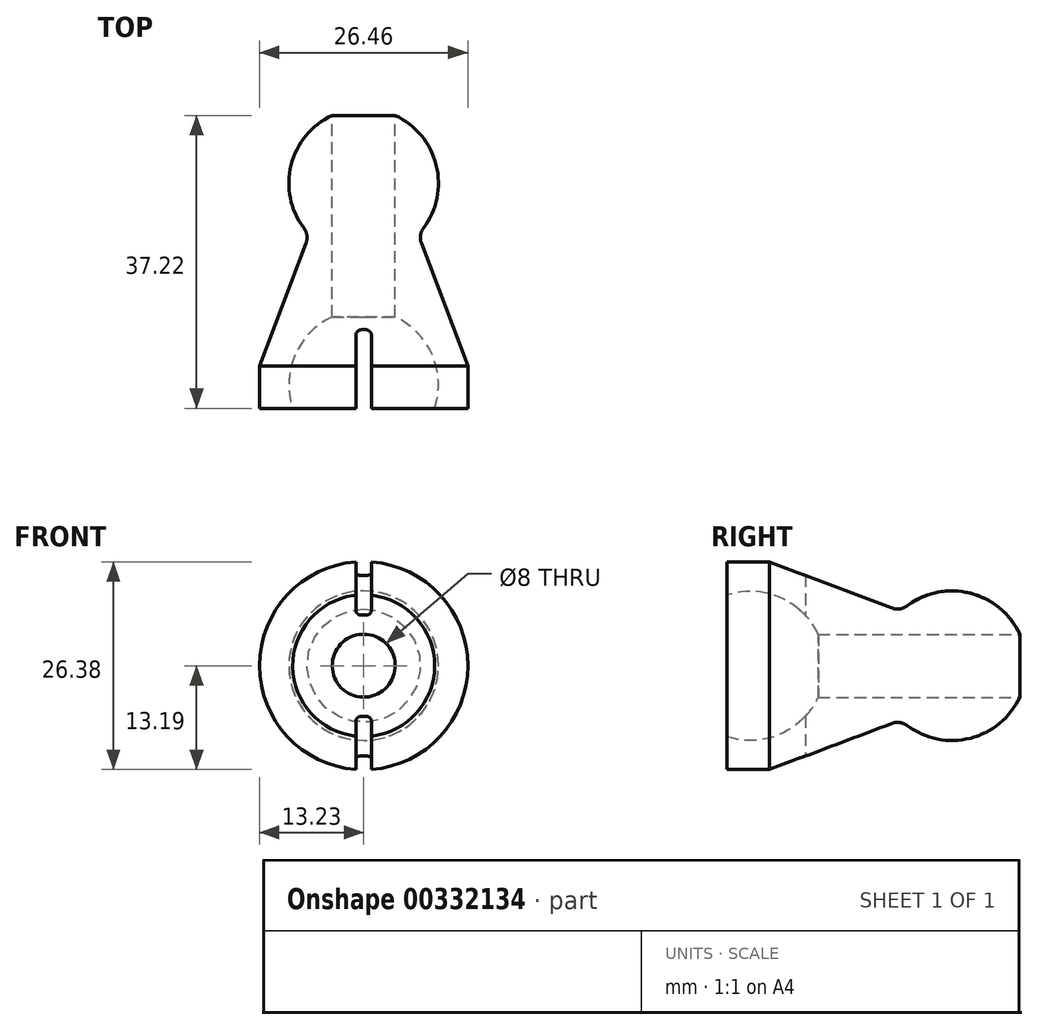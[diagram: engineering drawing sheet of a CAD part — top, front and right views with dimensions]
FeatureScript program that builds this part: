
annotation { "Feature Type Name" : "Feature", "Feature Type Description" : "" }
export const myFeature = defineFeature(function(context is Context, id is Id, definition is map)
    precondition{}
    {
        {
            var Q0;
            Q0=qCreatedBy(makeId("Top.planeOp"),FACE);
            var sketch = newSketch(context, id + "F0", { "sketchPlane" : qUnion([Q0])});
            skLineSegment(sketch, "E0", {"start": v(0, 38.1) * mm, "end": v(0, 0) * mm, "construction": true});
            skLineSegment(sketch, "E1", {"start": v(-4, 37.22) * mm, "end": v(-4, 11.62) * mm});
            skArc(sketch, "E2", {"start": v(-4, 37.22) * mm, "mid": v(-9.33, 30.4) * mm, "end": v(-6.9, 22.08) * mm});
            skLineSegment(sketch, "E3", {"start": v(-6.9, 22.08) * mm, "end": v(-13.23, 5.39) * mm});
            skLineSegment(sketch, "E4", {"start": v(-13.23, 0) * mm, "end": v(-9.01, 0) * mm});
            skPoint(sketch, "E5.orphan", {"position": v(-4, 38.1) * mm});
            skArc(sketch, "E6", {"start": v(-4, 11.62) * mm, "mid": v(-8.72, 6.76) * mm, "end": v(-9.01, 0) * mm});
            skPoint(sketch, "E7.start.orphan", {"position": v(-4, 0) * mm});
            skLineSegment(sketch, "E8", {"start": v(-13.23, 0) * mm, "end": v(-13.23, 5.39) * mm});
            skPoint(sketch, "E9.orphan", {"position": v(-15.27, 0) * mm});
            skSolve(sketch);
        }
        {
            var Q0;
            Q0=makeQuery(id+"F0.imprint","IMPRINT",FACE,{"disambiguationData":[TD([[makeQuery(id+"F0.imprint","IMPRINT",EDGE,{"derivedFrom":sQuery(id+"F0.wireOp",EDGE,"E1")}),-1.0]])]});
            var Q1;
            Q1=sQuery(id+"F0.wireOp",EDGE,"E0");
            revolve(context, id + "F1", {"entities" : qUnion([Q0]), "axis" : qUnion([Q1]), "revolveType" : RevolveType.FULL});
        }
        {
            var Q0;
            Q0=makeQuery(id+"F1.opRevolve","SWEPT_EDGE",EDGE,{"disambiguationData":[OSD([sQuery(id+"F0.wireOp",EDGE,"E2"),sQuery(id+"F0.wireOp",EDGE,"E3")])]});
            fillet(context, id + "F2", {"entities" : qUnion([Q0]), "radius" : 2 * mm, "tangentPropagation" : true, "allowEdgeOverflow" : false});
        }
        {
            var Q0;
            Q0=qCreatedBy(makeId("Top.planeOp"),FACE);
            var sketch = newSketch(context, id + "F3", { "sketchPlane" : qUnion([Q0])});
            skLineSegment(sketch, "E10.bottom", {"start": v(-1, 0) * mm, "end": v(1, 0) * mm});
            skLineSegment(sketch, "E10.top", {"start": v(-1, 10) * mm, "end": v(1, 10) * mm});
            skLineSegment(sketch, "E10.left", {"start": v(-1, 0) * mm, "end": v(-1, 10) * mm});
            skLineSegment(sketch, "E10.right", {"start": v(1, 0) * mm, "end": v(1, 10) * mm});
            skLineSegment(sketch, "E11.bottom", {"start": v(33.9, 36.66) * mm, "end": v(86.27, 36.66) * mm, "construction": true});
            skLineSegment(sketch, "E11.top", {"start": v(32.9, 6.55) * mm, "end": v(86.27, 6.55) * mm, "construction": true});
            skLineSegment(sketch, "E11.left", {"start": v(32.9, 35.66) * mm, "end": v(32.9, 6.55) * mm, "construction": true});
            skLineSegment(sketch, "E11.right", {"start": v(86.27, 36.66) * mm, "end": v(86.27, 6.55) * mm, "construction": true});
            skPoint(sketch, "E12.visualSharp", {"position": v(32.9, 36.66) * mm});
            skArc(sketch, "E12.filletArc", {"start": v(33.9, 36.66) * mm, "mid": v(33.19, 36.36) * mm, "end": v(32.9, 35.66) * mm, "construction": true});
            skSolve(sketch);
        }
        {
            var Q0;
            Q0=makeQuery(id+"F3.imprint","IMPRINT",FACE,{"disambiguationData":[TD([[makeQuery(id+"F3.imprint","IMPRINT",EDGE,{"derivedFrom":sQuery(id+"F3.wireOp",EDGE,"E10.bottom")}),1.0]])]});
            extrude(context, id + "F4", {"entities" : qUnion([Q0]), "operationType" : NewBodyOperationType.REMOVE, "endBound" : BoundingType.SYMMETRIC, "depth" : 33.6 * mm});
        }
        {
            var Q0;
            Q0=makeQuery(id+"F4.boolean.opBoolean","COPY",EDGE,{"disambiguationData":[OD(1.0)],"derivedFrom":makeQuery(id+"F4.opExtrude","SWEPT_EDGE",EDGE,{"disambiguationData":[OSD([sQuery(id+"F3.wireOp",EDGE,"E10.top"),sQuery(id+"F3.wireOp",EDGE,"E10.left")])]})});
            var Q1;
            Q1=makeQuery(id+"F4.boolean.opBoolean","COPY",EDGE,{"disambiguationData":[OD(1.0)],"derivedFrom":makeQuery(id+"F4.opExtrude","SWEPT_EDGE",EDGE,{"disambiguationData":[OSD([sQuery(id+"F3.wireOp",EDGE,"E10.top"),sQuery(id+"F3.wireOp",EDGE,"E10.right")])]})});
            var Q2;
            Q2=makeQuery(id+"F4.boolean.opBoolean","COPY",EDGE,{"disambiguationData":[OD(0.0)],"derivedFrom":makeQuery(id+"F4.opExtrude","SWEPT_EDGE",EDGE,{"disambiguationData":[OSD([sQuery(id+"F3.wireOp",EDGE,"E10.top"),sQuery(id+"F3.wireOp",EDGE,"E10.left")])]})});
            var Q3;
            Q3=makeQuery(id+"F4.boolean.opBoolean","COPY",EDGE,{"disambiguationData":[OD(0.0)],"derivedFrom":makeQuery(id+"F4.opExtrude","SWEPT_EDGE",EDGE,{"disambiguationData":[OSD([sQuery(id+"F3.wireOp",EDGE,"E10.top"),sQuery(id+"F3.wireOp",EDGE,"E10.right")])]})});
            fillet(context, id + "F5", {"entities" : qUnion([Q0, Q1, Q2, Q3]), "radius" : .75 * mm, "tangentPropagation" : true, "allowEdgeOverflow" : false});
        }
    });
